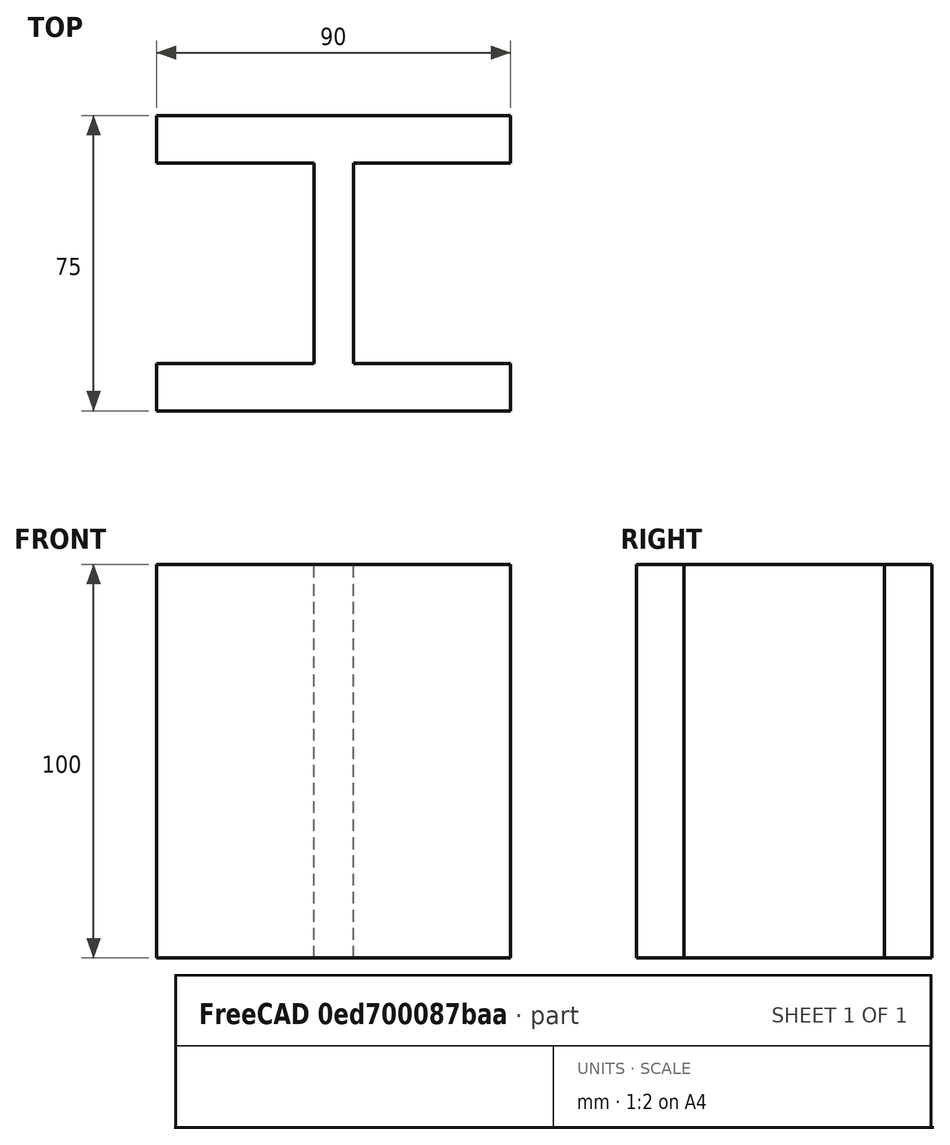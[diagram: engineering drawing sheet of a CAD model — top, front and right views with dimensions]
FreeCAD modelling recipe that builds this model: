
FCSTD DOCUMENT  (FreeCAD 0.17R13217 (Git))
Label: 02-Viga-H
License: All rights reserved
LicenseURL: http://en.wikipedia.org/wiki/All_rights_reserved
objects: Sketcher::SketchObject×1, PartDesign::Pad×1, PartDesign::Body×1
note: 4 computed .brp shape members not serialized (recipe doc carries the construction recipe); baked Part::Feature solids carry a one-line shape summary decoded from their .brp

FEATURE [Sketcher::SketchObject] Sketch
  MapMode = 5
  Support = -> [XY_Plane]
  sketch-geometry (12):
    g0: LineSegment StartX=0 StartY=75 StartZ=0 EndX=90 EndY=75 EndZ=0
    g1: LineSegment StartX=90 StartY=75 StartZ=0 EndX=90 EndY=63 EndZ=0
    g2: LineSegment StartX=90 StartY=63 StartZ=0 EndX=50 EndY=63 EndZ=0
    g3: LineSegment StartX=50 StartY=63 StartZ=0 EndX=50 EndY=12 EndZ=0
    g4: LineSegment StartX=50 StartY=12 StartZ=0 EndX=90 EndY=12 EndZ=0
    g5: LineSegment StartX=90 StartY=12 StartZ=0 EndX=90 EndY=0 EndZ=0
    g6: LineSegment StartX=90 StartY=0 StartZ=0 EndX=0 EndY=0 EndZ=0
    g7: LineSegment StartX=0 StartY=0 StartZ=0 EndX=0 EndY=12 EndZ=0
    g8: LineSegment StartX=0 StartY=12 StartZ=0 EndX=40 EndY=12 EndZ=0
    g9: LineSegment StartX=40 StartY=12 StartZ=0 EndX=40 EndY=63 EndZ=0
    g10: LineSegment StartX=40 StartY=63 StartZ=0 EndX=0 EndY=63 EndZ=0
    g11: LineSegment StartX=0 StartY=63 StartZ=0 EndX=0 EndY=75 EndZ=0
  constraints (36):
    c: Horizontal(g0)
    c: Coincident(g0,g1)
    c: Vertical(g1)
    c: Coincident(g1,g2)
    c: Horizontal(g2)
    c: Coincident(g2,g3)
    c: Vertical(g3)
    c: Coincident(g3,g4)
    c: Horizontal(g4)
    c: Coincident(g4,g5)
    c: Vertical(g5)
    c: Coincident(g5,g6)
    c: Horizontal(g6)
    c: Coincident(g6,g7)
    c: Vertical(g7)
    c: Coincident(g7,g8)
    c: Horizontal(g8)
    c: Coincident(g8,g9)
    c: Vertical(g9)
    c: Coincident(g9,g10)
    c: Horizontal(g10)
    c: Coincident(g10,g11)
    c: Coincident(g11,g0)
    c: Vertical(g11)
    c: Equal(g7,g5)
    c: Equal(g5,g1)
    c: Equal(g1,g11)
    c: DistanceY(g5,g5) = 12
    c: DistanceX(g9,g2) = 10
    c: Equal(g0,g6)
    c: Equal(g10,g8)
    c: Equal(g2,g4)
    c: DistanceX(g6,g6) = 90
    c: Equal(g10,g2)
    c: DistanceY(g6,g0) = 75
    c: Coincident(g6,g-1)
FEATURE [PartDesign::Pad] Pad
  Length = 100
  Length2 = 100
  Profile = -> Sketch
  Refine = true
  Type = 0
FEATURE [PartDesign::Body] Body
  Group = -> [Sketch,Pad]
  Origin = -> Origin
  Tip = -> Pad
